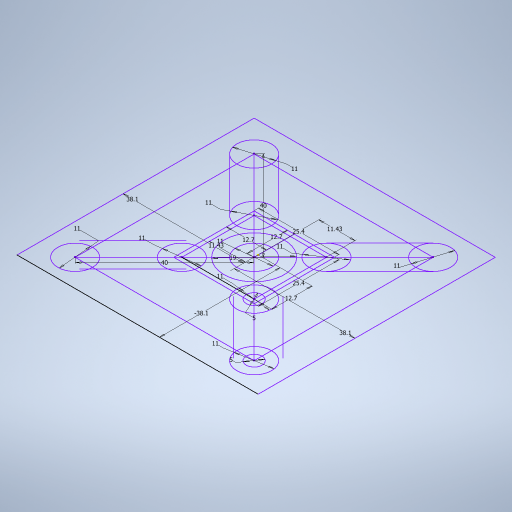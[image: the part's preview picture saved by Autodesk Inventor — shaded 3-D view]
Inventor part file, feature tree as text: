
AUTODESK INVENTOR PART (.ipt)
format: ipt  version: 2024 (Build 280153000, 153)  size: 275,968 bytes
history: native  units: in
note: dims shown in document units (in); Inventor stores cm internally (conversion verified against a paired STEP export)
features: sketch x1
ambient origin geometry x8: Origin, YZ Plane, XZ Plane, XY Plane, X Axis, Y Axis, Z Axis, Center Point
feature tree (1):
  sketch  "Sketch1"  dims[d0=1.0in d1=1.0in d2=0.5in d3=0.5in d4=1.5748in d5=1.5748in d7=0.45in d8=0.45in d9=0.4331in d10=0.4331in d11=0.4331in d12=0.4331in d13=0.4331in d14=0.4331in d15=0.4331in d16=0.4331in d18=-1.5in d19=1.5in d20=1.5in d21=0.748in d22=0.4331in d23=0.1969in d24=0.1969in d25=0.5in d26=0.0344in]
